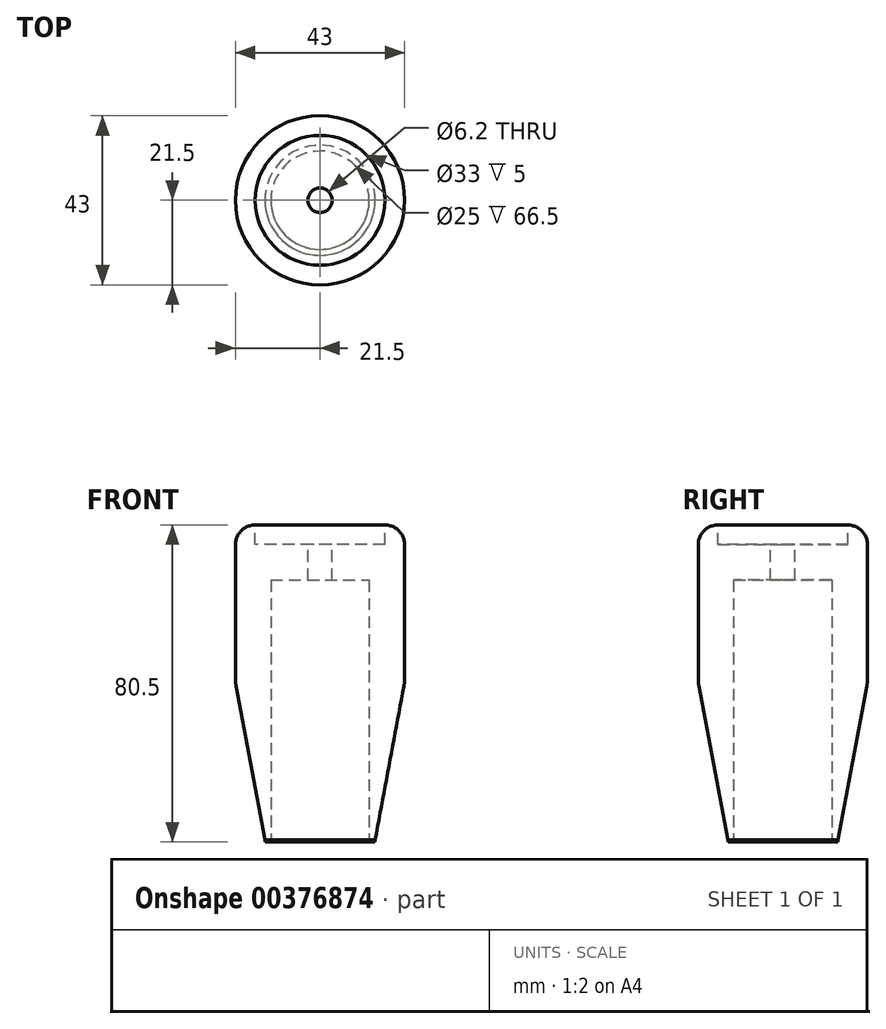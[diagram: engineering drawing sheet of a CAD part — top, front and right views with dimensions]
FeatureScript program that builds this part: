
annotation { "Feature Type Name" : "Feature", "Feature Type Description" : "" }
export const myFeature = defineFeature(function(context is Context, id is Id, definition is map)
    precondition{}
    {
        {
            var Q0;
            Q0=qCreatedBy(makeId("Top.planeOp"),FACE);
            var sketch = newSketch(context, id + "F0", { "sketchPlane" : qUnion([Q0])});
            skCircle(sketch, "E0", {"center": v(0, 0) * mm, "radius": 21.5 * mm});
            skSolve(sketch);
        }
        {
            var Q0;
            Q0=makeQuery(id+"F0.imprint","IMPRINT",FACE,{"disambiguationData":[TD([[makeQuery(id+"F0.imprint","IMPRINT",EDGE,{"derivedFrom":sQuery(id+"F0.wireOp",EDGE,"E0")}),1.0]])]});
            extrude(context, id + "F1", {"entities" : qUnion([Q0]), "depth" : 40 * mm});
        }
        {
            var Q0;
            Q0=makeQuery(id+"F1.opExtrude","CAP_EDGE",EDGE,{"disambiguationData":[OSD([sQuery(id+"F0.wireOp",EDGE,"E0")])],"isStart":false});
            fillet(context, id + "F2", {"entities" : qUnion([Q0]), "radius" : 5 * mm, "tangentPropagation" : true, "allowEdgeOverflow" : false});
        }
        {
            var Q0;
            Q0=makeQuery(id+"F1.opExtrude","CAP_FACE",FACE,{"disambiguationData":[OSD([sQuery(id+"F0.wireOp",EDGE,"E0")])],"isStart":true});
            var sketch = newSketch(context, id + "F3", { "sketchPlane" : qUnion([Q0])});
            skCircle(sketch, "E1", {"center": v(0, 0) * mm, "radius": 21.5 * mm});
            skSolve(sketch);
        }
        {
            var Q0;
            Q0=makeQuery(id+"F3.imprint","IMPRINT",FACE,{"disambiguationData":[TD([[makeQuery(id+"F3.imprint","IMPRINT",EDGE,{"derivedFrom":sQuery(id+"F3.wireOp",EDGE,"E1")}),-1.0]])]});
            extrude(context, id + "F4", {"entities" : qUnion([Q0]), "operationType" : NewBodyOperationType.ADD, "depth" : 40 * mm});
        }
        {
            var Q0;
            Q0=makeQuery(id+"F4.opExtrude","CAP_EDGE",EDGE,{"disambiguationData":[OSD([sQuery(id+"F3.wireOp",EDGE,"E1")])],"isStart":false});
            chamfer(context, id + "F5", {"entities" : qUnion([Q0]), "chamferType" : ChamferType.TWO_OFFSETS, "width1" : 40 * mm, "oppositeDirection" : false, "width2" : 7.5 * mm, "tangentPropagation" : true});
        }
        {
            var Q0;
            Q0=makeQuery(id+"F4.opExtrude","CAP_FACE",FACE,{"disambiguationData":[OSD([sQuery(id+"F3.wireOp",EDGE,"E1")])],"isStart":false});
            extrude(context, id + "F6", {"entities" : qUnion([Q0]), "operationType" : NewBodyOperationType.ADD, "depth" : 10 * mm});
        }
        {
            var Q0;
            {var subQ0=sQuery(id+"F3.wireOp",EDGE,"E1");Q0=makeQuery(id+"F5.opChamfer","BLEND_EDGE",EDGE,{"blendedFrom":[makeQuery(id+"F4.opExtrude","CAP_EDGE",EDGE,{"disambiguationData":[OSD([subQ0])],"isStart":false}),makeQuery(id+"F4.boolean.opBoolean","MERGE",FACE,{"derivedFrom":[makeQuery(id+"F1.opExtrude","SWEPT_FACE",FACE,{"disambiguationData":[OSD([sQuery(id+"F0.wireOp",EDGE,"E0")])]}),makeQuery(id+"F4.opExtrude","SWEPT_FACE",FACE,{"disambiguationData":[OSD([subQ0])]})]})],"blendedInto":[makeQuery(id+"F4.boolean.opBoolean","MERGE",FACE,{"derivedFrom":[makeQuery(id+"F1.opExtrude","SWEPT_FACE",FACE,{"disambiguationData":[OSD([sQuery(id+"F0.wireOp",EDGE,"E0")])]}),makeQuery(id+"F4.opExtrude","SWEPT_FACE",FACE,{"disambiguationData":[OSD([subQ0])]})]})]});}
            fillet(context, id + "F7", {"entities" : qUnion([Q0]), "radius" : 10 * mm, "tangentPropagation" : true, "allowEdgeOverflow" : false});
        }
        {
            var Q0;
            Q0=qCreatedBy(makeId("Right.planeOp"),FACE);
            var sketch = newSketch(context, id + "F8", { "sketchPlane" : qUnion([Q0])});
            skLineSegment(sketch, "E2.bottom", {"start": v(-17.43, -40.5) * mm, "end": v(-7.5, -40.5) * mm});
            skLineSegment(sketch, "E2.top", {"start": v(-10, -47.5) * mm, "end": v(-7.5, -47.5) * mm});
            skLineSegment(sketch, "E2.left", {"start": v(-17.43, -40.5) * mm, "end": v(-17.43, -47.5) * mm});
            skLineSegment(sketch, "E2.right", {"start": v(-7.5, -40.5) * mm, "end": v(-7.5, -47.5) * mm});
            skLineSegment(sketch, "E3", {"start": v(0, -39.98) * mm, "end": v(0, -66.82) * mm, "construction": true});
            skPoint(sketch, "E4.oppositeSnap0", {"position": v(-17.43, -44) * mm});
            skLineSegment(sketch, "E4.top", {"start": v(-10, -53.66) * mm, "end": v(-17.43, -53.66) * mm});
            skLineSegment(sketch, "E4.left", {"start": v(-10, -47.5) * mm, "end": v(-10, -53.66) * mm});
            skLineSegment(sketch, "E4.right", {"start": v(-17.43, -47.5) * mm, "end": v(-17.43, -53.66) * mm});
            skSolve(sketch);
        }
        {
            var Q0;
            Q0=makeQuery(id+"F8.imprint","IMPRINT",FACE,{"disambiguationData":[TD([[makeQuery(id+"F8.imprint","IMPRINT",EDGE,{"derivedFrom":sQuery(id+"F8.wireOp",EDGE,"E2.bottom")}),-1.0]])]});
            var Q1;
            Q1=sQuery(id+"F8.wireOp",EDGE,"E3");
            revolve(context, id + "F9", {"operationType" : NewBodyOperationType.REMOVE, "entities" : qUnion([Q0]), "axis" : qUnion([Q1]), "revolveType" : RevolveType.FULL, "oppositeDirection" : true});
        }
        {
            var Q0;
            Q0=makeQuery(id+"F6.opExtrude","CAP_FACE",FACE,{"disambiguationData":[OSD([sQuery(id+"F3.wireOp",EDGE,"E1")])],"isStart":false});
            var sketch = newSketch(context, id + "F10", { "sketchPlane" : qUnion([Q0])});
            skCircle(sketch, "E5", {"center": v(0, 0) * mm, "radius": 4.9 * mm});
            skSolve(sketch);
        }
        {
            var Q0;
            Q0=makeQuery(id+"F10.imprint","IMPRINT",FACE,{"disambiguationData":[TD([[makeQuery(id+"F10.imprint","IMPRINT",EDGE,{"derivedFrom":sQuery(id+"F10.wireOp",EDGE,"E5")}),1.0]])]});
            extrude(context, id + "F11", {"entities" : qUnion([Q0]), "operationType" : NewBodyOperationType.REMOVE, "oppositeDirection" : true, "depth" : 75 * mm});
        }
        {
            var Q0;
            Q0=makeQuery(id+"F1.opExtrude","CAP_FACE",FACE,{"disambiguationData":[OSD([sQuery(id+"F0.wireOp",EDGE,"E0")])],"isStart":false});
            var sketch = newSketch(context, id + "F12", { "sketchPlane" : qUnion([Q0])});
            skCircle(sketch, "E6", {"center": v(0, 0) * mm, "radius": 16.5 * mm});
            skSolve(sketch);
        }
        {
            var Q0;
            Q0=makeQuery(id+"F12.imprint","IMPRINT",FACE,{"disambiguationData":[TD([[makeQuery(id+"F12.imprint","IMPRINT",EDGE,{"derivedFrom":sQuery(id+"F12.wireOp",EDGE,"E6")}),1.0]])]});
            extrude(context, id + "F13", {"entities" : qUnion([Q0]), "operationType" : NewBodyOperationType.REMOVE, "oppositeDirection" : true, "depth" : 5 * mm});
        }
        {
            var Q0;
            Q0=makeQuery(id+"F13.boolean.opBoolean","COPY",FACE,{"derivedFrom":makeQuery(id+"F13.opExtrude","CAP_FACE",FACE,{"disambiguationData":[OSD([sQuery(id+"F12.wireOp",EDGE,"E6")])],"isStart":false})});
            var sketch = newSketch(context, id + "F14", { "sketchPlane" : qUnion([Q0])});
            skCircle(sketch, "E7", {"center": v(0, 0) * mm, "radius": 3.1 * mm});
            skSolve(sketch);
        }
        {
            var Q0;
            Q0=makeQuery(id+"F14.imprint","IMPRINT",FACE,{"disambiguationData":[TD([[makeQuery(id+"F14.imprint","IMPRINT",EDGE,{"derivedFrom":sQuery(id+"F14.wireOp",EDGE,"E7")}),1.0]])]});
            extrude(context, id + "F15", {"entities" : qUnion([Q0]), "operationType" : NewBodyOperationType.REMOVE, "endBound" : BoundingType.THROUGH_ALL, "oppositeDirection" : true, "depth" : 25 * mm});
        }
        {
            var Q0;
            Q0=makeQuery(id+"F6.opExtrude","CAP_FACE",FACE,{"disambiguationData":[OSD([sQuery(id+"F3.wireOp",EDGE,"E1")])],"isStart":false});
            var sketch = newSketch(context, id + "F16", { "sketchPlane" : qUnion([Q0])});
            skCircle(sketch, "E8", {"center": v(0, 0) * mm, "radius": 12.5 * mm});
            skSolve(sketch);
        }
        {
            var Q0;
            Q0 = qSketchRegion(id + "F16", true);
            extrude(context, id + "F17", {"entities" : qUnion([Q0]), "operationType" : NewBodyOperationType.REMOVE, "oppositeDirection" : true, "depth" : 76 * mm});
        }
    });
